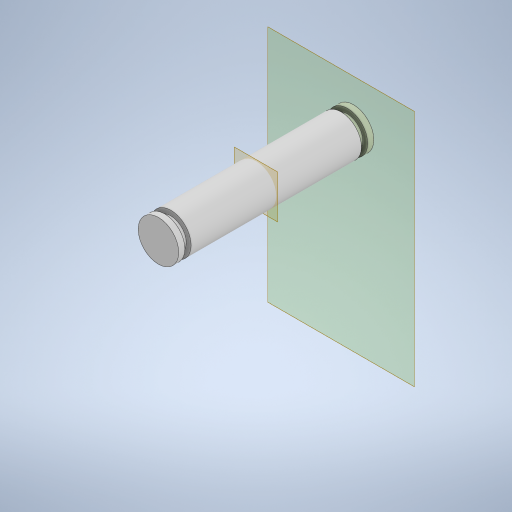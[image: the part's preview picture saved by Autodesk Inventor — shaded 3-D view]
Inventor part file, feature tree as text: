
AUTODESK INVENTOR PART (.ipt)
format: ipt  version: 2024 (Build 280153000, 153)  size: 617,984 bytes
history: native  units: mm
features: other x4, plane x3, sketch x3, extrude x3, mirror x1, reference x1, projected_geometry x1
ambient origin geometry x8: Origin, YZ Plane, XZ Plane, XY Plane, X Axis, Y Axis, Z Axis, Center Point
bodies: Solid1 (feature_tree)
feature tree (16):
  plane  "Work Plane1"
  sketch  "Sketch1"  dims[d0=10.0mm d1=0.0mm d2=0.41mm]
  plane  "Work Plane2"
  extrude  "Extrusion1"  Depth=10.0mm
  extrude  "Extrusion2"  Depth=4.0mm TaperAngle=0.0deg
  extrude  "Extrusion3"  [1 undecoded]
  plane  "Work Plane3"
  mirror  "Mirror1"
  reference  "Reference1"
  sketch  "Sketch2"  dims[d3=20.0mm d4=4.0mm d5=0.0mm]
  projected_geometry  "Projected Loop1"
  sketch  "Sketch3"  dims[d6=4.0mm d7=0.0mm]
  other  "<userpath>\Documents\Inventor\robot arm\arms\arms.iam"
  other  "arms.iam"
  other  "arm-bearings:3"
  other  "base:1"
note: 1 required parameter value undecoded (feature->parameter linkage not recoverable at this tier; creation-order binding heuristic only, values carry confidence <= 0.55)
